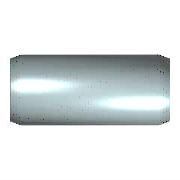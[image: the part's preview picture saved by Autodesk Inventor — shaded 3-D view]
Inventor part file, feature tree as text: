
AUTODESK INVENTOR PART (.ipt)
format: ipt  version: 2023.3 (Build 273359000, 359)  size: 114,688 bytes
history: native  units: mm (DEFAULTED — no unit token found)
features: extrude x1, sketch x1
ambient origin geometry x8: Origin, YZ Plane, XZ Plane, XY Plane, X Axis, Y Axis, Z Axis, Center Point
bodies: Solid1 (feature_tree)
feature tree (2):
  extrude  "Körper"  Depth=14.0mm
  sketch  "Skizze"  dims[d1=2.5mm d2=14.0mm d3=0.0mm d4=0.4mm d5=15.0deg d8=0.4mm d9=15.0deg d11=0.4mm d12=0.4mm d13=0.0mm d15=0.0mm d16=0.0mm]
